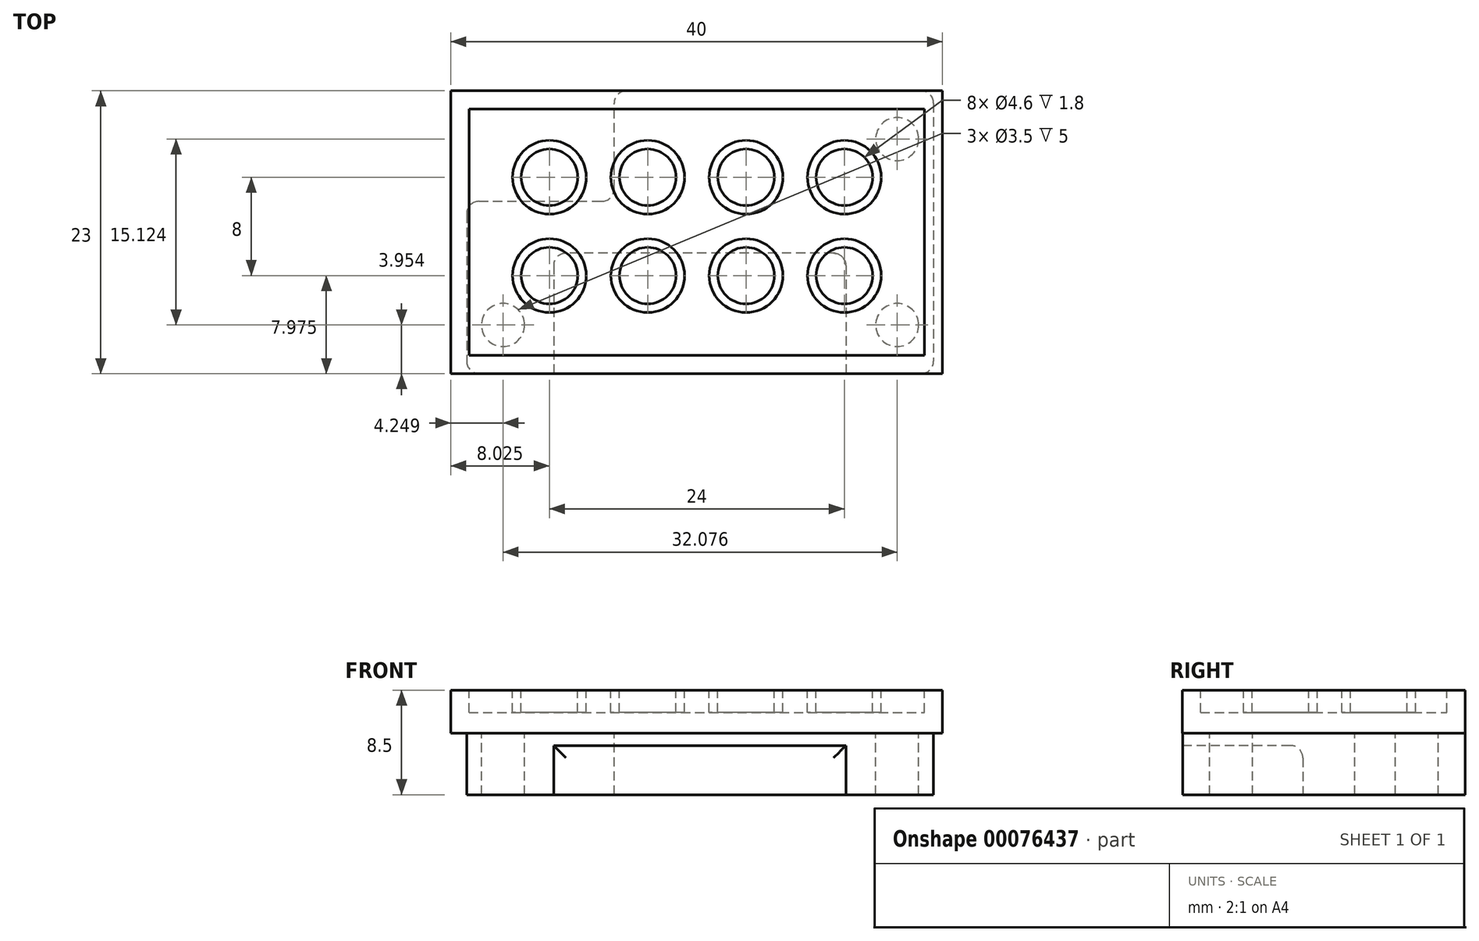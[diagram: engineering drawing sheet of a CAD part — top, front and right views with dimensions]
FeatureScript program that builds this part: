
annotation { "Feature Type Name" : "Feature", "Feature Type Description" : "" }
export const myFeature = defineFeature(function(context is Context, id is Id, definition is map)
    precondition{}
    {
        {
            var Q0;
            Q0=qCreatedBy(makeId("Top.planeOp"),FACE);
            var sketch = newSketch(context, id + "F0", { "sketchPlane" : qUnion([Q0])});
            skLineSegment(sketch, "E0.bottom", {"start": v(0, 0) * mm, "end": v(-40, 0) * mm});
            skLineSegment(sketch, "E0.top", {"start": v(0, 23) * mm, "end": v(-40, 23) * mm});
            skLineSegment(sketch, "E0.left", {"start": v(0, 0) * mm, "end": v(0, 23) * mm});
            skLineSegment(sketch, "E0.right", {"start": v(-40, 0) * mm, "end": v(-40, 23) * mm});
            skSolve(sketch);
        }
        {
            var Q0;
            Q0=makeQuery(id+"F0.imprint","IMPRINT",FACE,{"disambiguationData":[TD([[makeQuery(id+"F0.imprint","IMPRINT",EDGE,{"derivedFrom":sQuery(id+"F0.wireOp",EDGE,"E0.bottom")}),-1.0]])]});
            extrude(context, id + "F1", {"entities" : qUnion([Q0]), "oppositeDirection" : true, "depth" : 3.5 * mm});
        }
        {
            var Q0;
            Q0=qCreatedBy(makeId("Top.planeOp"),FACE);
            var sketch = newSketch(context, id + "F2", { "sketchPlane" : qUnion([Q0])});
            skLineSegment(sketch, "E1.bottom", {"start": v(-38.52, 1.48) * mm, "end": v(-1.47, 1.48) * mm});
            skLineSegment(sketch, "E1.top", {"start": v(-38.52, 21.52) * mm, "end": v(-1.47, 21.53) * mm});
            skLineSegment(sketch, "E1.left", {"start": v(-38.52, 1.48) * mm, "end": v(-38.52, 21.52) * mm});
            skLineSegment(sketch, "E1.right", {"start": v(-1.47, 1.48) * mm, "end": v(-1.47, 21.53) * mm});
            skCircle(sketch, "E2", {"center": v(-7.97, 7.98) * mm, "radius": 3 * mm});
            skCircle(sketch, "E3.0.1.0", {"center": v(-7.97, 15.98) * mm, "radius": 3 * mm});
            skCircle(sketch, "E3.1.0.0", {"center": v(-15.97, 7.98) * mm, "radius": 3 * mm});
            skCircle(sketch, "E3.1.1.0", {"center": v(-15.97, 15.98) * mm, "radius": 3 * mm});
            skCircle(sketch, "E3.2.0.0", {"center": v(-23.97, 7.98) * mm, "radius": 3 * mm});
            skCircle(sketch, "E3.2.1.0", {"center": v(-23.97, 15.98) * mm, "radius": 3 * mm});
            skCircle(sketch, "E3.3.0.0", {"center": v(-31.97, 7.98) * mm, "radius": 3 * mm});
            skCircle(sketch, "E3.3.1.0", {"center": v(-31.97, 15.98) * mm, "radius": 3 * mm});
            skLineSegment(sketch, "E3.direction1", {"start": v(-7.97, 7.98) * mm, "end": v(-15.97, 7.98) * mm, "construction": true});
            skLineSegment(sketch, "E3.direction2", {"start": v(-7.97, 7.98) * mm, "end": v(-7.97, 15.98) * mm, "construction": true});
            skSolve(sketch);
        }
        {
            var Q0;
            {var subQ0=sQuery(id+"F0.wireOp",EDGE,"E0.bottom");var subQ1=sQuery(id+"F0.wireOp",EDGE,"E0.top");var subQ2=sQuery(id+"F0.wireOp",EDGE,"E0.left");var subQ3=sQuery(id+"F0.wireOp",EDGE,"E0.right");Q0=makeQuery(id+"F4.boolean.opBoolean","SPLIT",FACE,{"disambiguationData":[TD([makeQuery(id+"F1.opExtrude","SWEPT_FACE",FACE,{"disambiguationData":[OSD([subQ0])]})])],"derivedFrom":makeQuery(id+"F1.opExtrude","CAP_FACE",FACE,{"disambiguationData":[OSD([subQ0,subQ1,subQ2,subQ3])],"isStart":true})});}
            var sketch = newSketch(context, id + "F3", { "sketchPlane" : qUnion([Q0])});
            skCircle(sketch, "E4", {"center": v(-7.98, 7.97) * mm, "radius": 2.3 * mm});
            skCircle(sketch, "E5.0.1.0", {"center": v(-7.98, 15.97) * mm, "radius": 2.3 * mm});
            skCircle(sketch, "E5.1.0.0", {"center": v(-15.98, 7.97) * mm, "radius": 2.3 * mm});
            skCircle(sketch, "E5.1.1.0", {"center": v(-15.98, 15.97) * mm, "radius": 2.3 * mm});
            skCircle(sketch, "E5.2.0.0", {"center": v(-23.98, 7.97) * mm, "radius": 2.3 * mm});
            skCircle(sketch, "E5.2.1.0", {"center": v(-23.98, 15.97) * mm, "radius": 2.3 * mm});
            skCircle(sketch, "E5.3.0.0", {"center": v(-31.98, 7.97) * mm, "radius": 2.3 * mm});
            skCircle(sketch, "E5.3.1.0", {"center": v(-31.98, 15.97) * mm, "radius": 2.3 * mm});
            skLineSegment(sketch, "E5.direction1", {"start": v(-7.98, 7.97) * mm, "end": v(-15.98, 7.97) * mm, "construction": true});
            skLineSegment(sketch, "E5.direction2", {"start": v(-7.98, 7.97) * mm, "end": v(-7.98, 15.97) * mm, "construction": true});
            skSolve(sketch);
        }
        {
            var Q0;
            Q0=qSketchRegion(id+"F2",true);
            var Q1;
            Q1=qSketchRegion(id+"F3",true);
            var Q2;
            Q2=sQuery(id+"F2.wireOp",EDGE,"de4b574f-d5fe-483e-a269-1c24a673af37.0.MirrorC");
            extrude(context, id + "F4", {"entities" : qUnion([Q0, Q1]), "operationType" : NewBodyOperationType.REMOVE, "surfaceEntities" : qUnion([Q2]), "oppositeDirection" : true, "depth" : 1.8 * mm});
        }
        {
            var Q0;
            Q0=makeQuery(id+"F1.opExtrude","CAP_FACE",FACE,{"disambiguationData":[OSD([sQuery(id+"F0.wireOp",EDGE,"E0.bottom"),sQuery(id+"F0.wireOp",EDGE,"E0.top"),sQuery(id+"F0.wireOp",EDGE,"E0.left"),sQuery(id+"F0.wireOp",EDGE,"E0.right")])],"isStart":false});
            var sketch = newSketch(context, id + "F5", { "sketchPlane" : qUnion([Q0])});
            skLineSegment(sketch, "E6.bottom", {"start": v(-0.71, -23.02) * mm, "end": v(-26.71, -23.02) * mm});
            skLineSegment(sketch, "E6.top", {"start": v(-0.71, -0.02) * mm, "end": v(-38.71, -0.02) * mm});
            skLineSegment(sketch, "E6.left", {"start": v(-0.71, -23.02) * mm, "end": v(-0.71, -0.02) * mm});
            skLineSegment(sketch, "E6.right", {"start": v(-38.71, -14.02) * mm, "end": v(-38.71, -0.02) * mm});
            skPoint(sketch, "E6.middle", {"position": v(-19.71, -11.52) * mm});
            skCircle(sketch, "E7", {"center": v(-3.68, -3.95) * mm, "radius": 1.75 * mm});
            skCircle(sketch, "E8.MirrorC", {"center": v(-3.68, -19.08) * mm, "radius": 1.75 * mm});
            skCircle(sketch, "E9.MirrorC", {"center": v(-35.75, -3.95) * mm, "radius": 1.75 * mm});
            skLineSegment(sketch, "E10.bottom", {"start": v(-38.71, -14.02) * mm, "end": v(-26.71, -14.02) * mm});
            skLineSegment(sketch, "E10.right", {"start": v(-26.71, -14.02) * mm, "end": v(-26.71, -23.02) * mm});
            skPoint(sketch, "E11.orphan", {"position": v(-38.71, -23.02) * mm});
            skPoint(sketch, "E12.end.orphan", {"position": v(-19.71, -23.02) * mm});
            skPoint(sketch, "E13.end.orphan", {"position": v(-19.71, -0.02) * mm});
            skSolve(sketch);
        }
        {
            var Q0;
            {var subQ1=sQuery(id+"F5.wireOp",EDGE,"E6.top");Q0=makeQuery(id+"F5.imprint","IMPRINT",FACE,{"disambiguationData":[TD([[makeQuery(id+"F5.imprint","IMPRINT",EDGE,{"derivedFrom":subQ1}),1.0]])]});}
            extrude(context, id + "F6", {"entities" : qUnion([Q0]), "operationType" : NewBodyOperationType.ADD, "depth" : 5 * mm});
        }
        {
            var Q0;
            Q0=makeQuery(id+"F6.opExtrude","CAP_FACE",FACE,{"disambiguationData":[OSD([sQuery(id+"F0.wireOp",EDGE,"E0.top"),sQuery(id+"F5.wireOp",EDGE,"E6.top"),sQuery(id+"F5.wireOp",EDGE,"E6.left"),sQuery(id+"F5.wireOp",EDGE,"E6.right"),sQuery(id+"F5.wireOp",EDGE,"E7"),sQuery(id+"F5.wireOp",EDGE,"E8.MirrorC"),sQuery(id+"F5.wireOp",EDGE,"E9.MirrorC"),sQuery(id+"F5.wireOp",EDGE,"E10.bottom"),sQuery(id+"F5.wireOp",EDGE,"E10.right")])],"isStart":false});
            var sketch = newSketch(context, id + "F7", { "sketchPlane" : qUnion([Q0])});
            skLineSegment(sketch, "E14.bottom", {"start": v(-7.86, -9.8) * mm, "end": v(-31.63, -9.8) * mm});
            skLineSegment(sketch, "E14.top", {"start": v(-7.86, -0.02) * mm, "end": v(-31.63, -0.02) * mm});
            skLineSegment(sketch, "E14.left", {"start": v(-7.86, -9.8) * mm, "end": v(-7.86, -0.02) * mm});
            skLineSegment(sketch, "E14.right", {"start": v(-31.63, -9.8) * mm, "end": v(-31.63, -0.02) * mm});
            skSolve(sketch);
        }
        {
            var Q0;
            Q0=qSketchRegion(id+"F7",true);
            extrude(context, id + "F8", {"entities" : qUnion([Q0]), "operationType" : NewBodyOperationType.REMOVE, "oppositeDirection" : true, "depth" : 4 * mm});
        }
        {
            var Q0;
            Q0=makeQuery(id+"F8.boolean.opBoolean","COPY",EDGE,{"derivedFrom":makeQuery(id+"F8.opExtrude","SWEPT_EDGE",EDGE,{"disambiguationData":[OSD([sQuery(id+"F7.wireOp",EDGE,"E14.bottom"),sQuery(id+"F7.wireOp",EDGE,"E14.right")])]})});
            var Q1;
            Q1=makeQuery(id+"F8.boolean.opBoolean","COPY",EDGE,{"derivedFrom":makeQuery(id+"F8.opExtrude","SWEPT_EDGE",EDGE,{"disambiguationData":[OSD([sQuery(id+"F7.wireOp",EDGE,"E14.bottom"),sQuery(id+"F7.wireOp",EDGE,"E14.left")])]})});
            var Q2;
            Q2=makeQuery(id+"F6.opExtrude","SWEPT_EDGE",EDGE,{"disambiguationData":[OSD([sQuery(id+"F5.wireOp",EDGE,"E10.bottom"),sQuery(id+"F5.wireOp",EDGE,"E10.right")])]});
            var Q3;
            Q3=makeQuery(id+"F8.boolean.opBoolean","COPY",EDGE,{"derivedFrom":makeQuery(id+"F8.opExtrude","CAP_EDGE",EDGE,{"disambiguationData":[OSD([sQuery(id+"F7.wireOp",EDGE,"E14.bottom")])],"isStart":false})});
            var Q4;
            Q4=makeQuery(id+"F6.opExtrude","SWEPT_EDGE",EDGE,{"disambiguationData":[OSD([sQuery(id+"F5.wireOp",EDGE,"E6.top"),sQuery(id+"F5.wireOp",EDGE,"E6.left")])]});
            var Q5;
            Q5=makeQuery(id+"F6.opExtrude","SWEPT_EDGE",EDGE,{"disambiguationData":[OSD([sQuery(id+"F5.wireOp",EDGE,"E6.top"),sQuery(id+"F5.wireOp",EDGE,"E6.right")])]});
            var Q6;
            Q6=makeQuery(id+"F6.opExtrude","SWEPT_EDGE",EDGE,{"disambiguationData":[OSD([sQuery(id+"F5.wireOp",EDGE,"E6.right"),sQuery(id+"F5.wireOp",EDGE,"E10.bottom")])]});
            var Q7;
            Q7=makeQuery(id+"F6.opExtrude","SWEPT_EDGE",EDGE,{"disambiguationData":[OSD([sQuery(id+"F0.wireOp",EDGE,"E0.top"),sQuery(id+"F5.wireOp",EDGE,"E10.right")])]});
            var Q8;
            Q8=makeQuery(id+"F6.opExtrude","SWEPT_EDGE",EDGE,{"disambiguationData":[OSD([sQuery(id+"F0.wireOp",EDGE,"E0.top"),sQuery(id+"F5.wireOp",EDGE,"E6.left")])]});
            fillet(context, id + "F9", {"entities" : qUnion([Q0, Q1, Q2, Q3, Q4, Q5, Q6, Q7, Q8]), "radius" : 1 * mm, "tangentPropagation" : true, "allowEdgeOverflow" : false});
        }
    });
